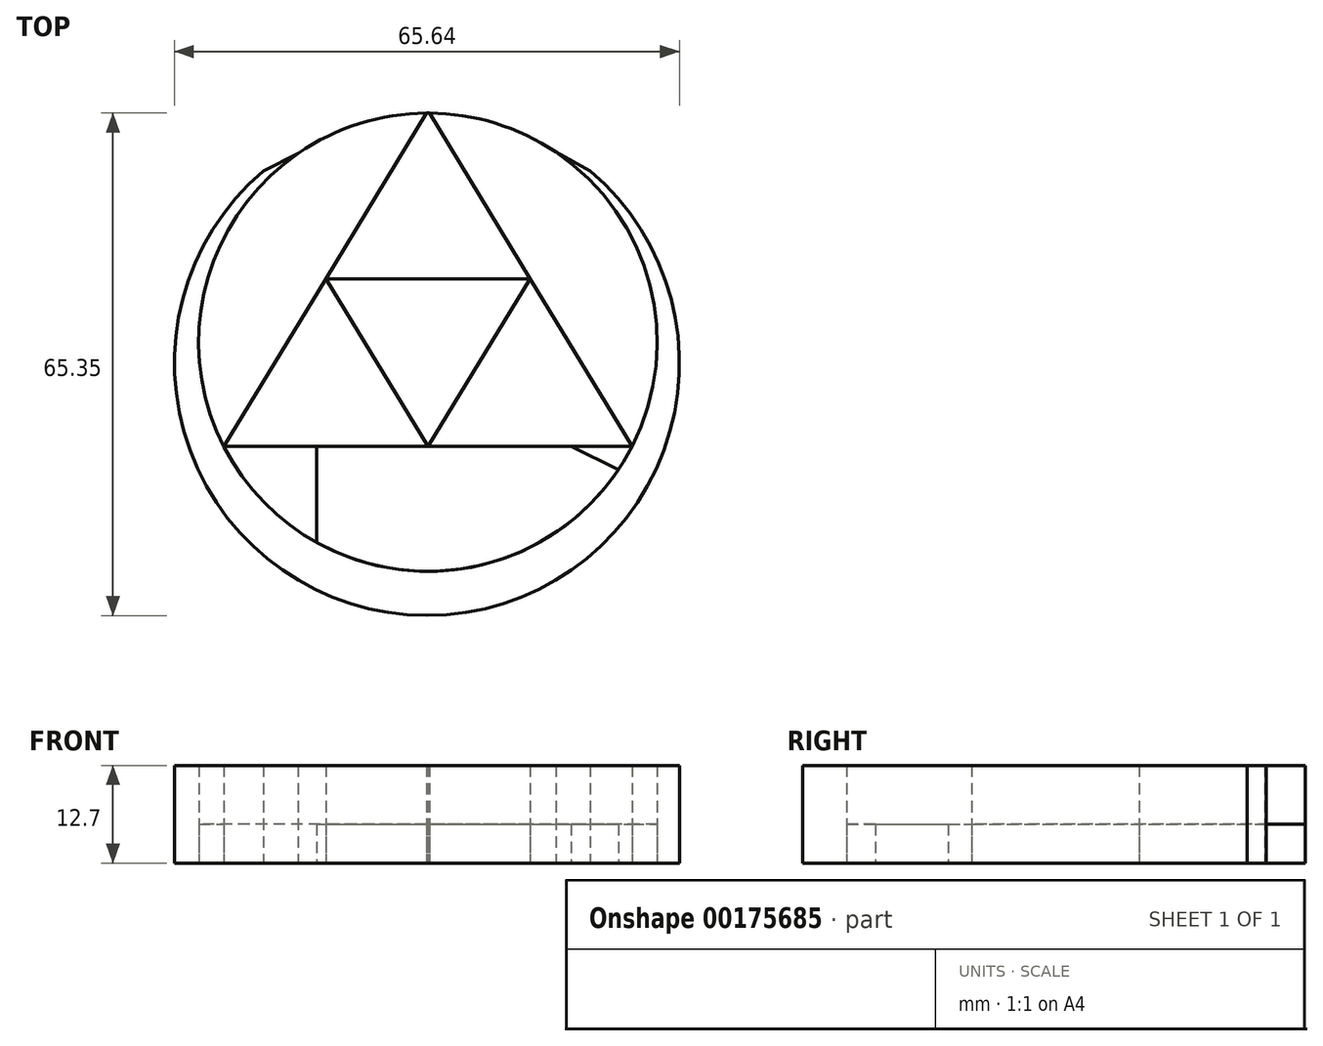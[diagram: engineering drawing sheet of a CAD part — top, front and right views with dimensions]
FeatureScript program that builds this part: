
annotation { "Feature Type Name" : "Feature", "Feature Type Description" : "" }
export const myFeature = defineFeature(function(context is Context, id is Id, definition is map)
    precondition{}
    {
        {
            var Q0;
            Q0=qCreatedBy(makeId("Top.planeOp"),FACE);
            var sketch = newSketch(context, id + "F0", { "sketchPlane" : qUnion([Q0])});
            skCircle(sketch, "E0", {"center": v(-14, 9.39) * mm, "radius": 29.8 * mm});
            skLineSegment(sketch, "E1", {"start": v(-40.55, -4.17) * mm, "end": v(12.54, -4.17) * mm});
            skLineSegment(sketch, "E2.bottom", {"start": v(-40.55, -4.17) * mm, "end": v(12.55, -4.17) * mm});
            skLineSegment(sketch, "E2.right", {"start": v(12.55, -4.17) * mm, "end": v(12.55, -4.16) * mm});
            skLineSegment(sketch, "E3", {"start": v(-14, 39.48) * mm, "end": v(-40.55, -4.17) * mm});
            skLineSegment(sketch, "E4", {"start": v(-14, 39.48) * mm, "end": v(12.54, -4.17) * mm});
            skPoint(sketch, "E5.orphan", {"position": v(-40.55, 39.48) * mm});
            skPoint(sketch, "E6.orphan", {"position": v(12.54, 39.48) * mm});
            skLineSegment(sketch, "E7", {"start": v(-27.27, 17.66) * mm, "end": v(-0.73, 17.66) * mm});
            skLineSegment(sketch, "E8", {"start": v(-0.73, 17.66) * mm, "end": v(-14, -4.17) * mm});
            skLineSegment(sketch, "E9", {"start": v(-14, -4.17) * mm, "end": v(-27.27, 17.66) * mm});
            skArc(sketch, "E10", {"start": v(-35.38, 31.68) * mm, "mid": v(-14.14, -26.16) * mm, "end": v(7.1, 31.68) * mm});
            skPoint(sketch, "E10.second.point", {"position": v(-14, -26.16) * mm});
            skPoint(sketch, "E10.third.point", {"position": v(15.75, -6.9) * mm});
            skPoint(sketch, "E11.middle", {"position": v(-14, -20.42) * mm});
            skPoint(sketch, "E12.orphan", {"position": v(-24.56, 2.87) * mm});
            skLineSegment(sketch, "E13.trimOffspring", {"start": v(-24.56, -4.17) * mm, "end": v(-24.56, -4.17) * mm});
            skLineSegment(sketch, "E14.trimOffspring", {"start": v(-3.44, -4.17) * mm, "end": v(-3.44, -4.17) * mm});
            skPoint(sketch, "E15.trimOffspring.end.orphan", {"position": v(-3.44, 2.87) * mm});
            skPoint(sketch, "E11.bottom.start.orphan", {"position": v(-24.56, -43.7) * mm});
            skPoint(sketch, "E11.right.start.orphan", {"position": v(-3.44, -43.7) * mm});
            skLineSegment(sketch, "E16.left", {"start": v(-10.35, -56.05) * mm, "end": v(-9.1, -67.57) * mm});
            skLineSegment(sketch, "E16.right", {"start": v(-19.53, -55.34) * mm, "end": v(-18.29, -66.87) * mm});
            skPoint(sketch, "E16.middle", {"position": v(-14.32, -61.46) * mm});
            skPoint(sketch, "E16.cornerSnap0", {"position": v(-28.46, -56.05) * mm});
            skPoint(sketch, "E17.orphan", {"position": v(-28.46, -61.9) * mm});
            skPoint(sketch, "E18.orphan", {"position": v(-0.18, -61.01) * mm});
            skLineSegment(sketch, "E19", {"start": v(-35.38, 31.68) * mm, "end": v(-30.87, 33.96) * mm});
            skLineSegment(sketch, "E20", {"start": v(7.1, 31.68) * mm, "end": v(2.63, 34.12) * mm});
            skPoint(sketch, "E21.middle", {"position": v(-13.7, -67.22) * mm});
            skPoint(sketch, "E21.right.end.orphan", {"position": v(-22.4, -64) * mm});
            skPoint(sketch, "E21.left.end.orphan", {"position": v(-5.12, -63.93) * mm});
            skPoint(sketch, "E21.bottom.end.orphan", {"position": v(-22.28, -70.52) * mm});
            skPoint(sketch, "E21.bottom.start.orphan", {"position": v(-5, -70.45) * mm});
            skLineSegment(sketch, "E22", {"start": v(-18.29, -66.87) * mm, "end": v(-22.28, -70.52) * mm});
            skLineSegment(sketch, "E23", {"start": v(-9.1, -67.57) * mm, "end": v(-5, -70.45) * mm});
            skLineSegment(sketch, "E24", {"start": v(-5, -70.45) * mm, "end": v(-13.7, -102.19) * mm});
            skLineSegment(sketch, "E25", {"start": v(-13.7, -102.19) * mm, "end": v(-22.28, -70.52) * mm});
            skLineSegment(sketch, "E26.right", {"start": v(-28.47, -16.67) * mm, "end": v(-28.47, -2.12) * mm});
            skLineSegment(sketch, "E27.trimOffspring", {"start": v(10.76, -7.2) * mm, "end": v(0.46, -2.12) * mm});
            skPoint(sketch, "E26.bottom.end.orphan", {"position": v(-28.46, -50.2) * mm});
            skPoint(sketch, "E26.bottom.start.orphan", {"position": v(0.46, -50.2) * mm});
            skLineSegment(sketch, "E28", {"start": v(-19.53, -55.34) * mm, "end": v(-28.46, -50.2) * mm});
            skLineSegment(sketch, "E29", {"start": v(-14, -26.16) * mm, "end": v(-28.46, -50.2) * mm});
            skLineSegment(sketch, "E30", {"start": v(0.46, -50.2) * mm, "end": v(-14, -26.16) * mm});
            skLineSegment(sketch, "E31", {"start": v(0.46, -50.2) * mm, "end": v(-10.35, -56.05) * mm});
            skPoint(sketch, "E32.right.end.orphan", {"position": v(-0.18, -45.42) * mm});
            skSolve(sketch);
        }
        {
            var Q0;
            {var subQ5=sQuery(id+"F0.wireOp",EDGE,"E7");Q0=makeQuery(id+"F0.imprint","IMPRINT",FACE,{"disambiguationData":[TD([[makeQuery(id+"F0.imprint","IMPRINT",EDGE,{"derivedFrom":subQ5}),1.0]])]});}
            var Q1;
            {var subQ1=sQuery(id+"F0.wireOp",EDGE,"E1");var subQ3=makeQuery(id+"F0.imprint","INTERSECT",VERTEX,{"derivedFrom":[subQ1,sQuery(id+"F0.wireOp",EDGE,"E13.trimOffspring")]});Q1=makeQuery(id+"F0.imprint","IMPRINT",FACE,{"disambiguationData":[TD([[makeQuery(id+"F0.imprint","IMPRINT",EDGE,{"disambiguationData":[TD([[subQ3,-1.0]])],"derivedFrom":subQ1}),1.0]])]});}
            var Q2;
            {var subQ0=sQuery(id+"F0.wireOp",EDGE,"E1");var subQ1=makeQuery(id+"F0.imprint","INTERSECT",VERTEX,{"derivedFrom":[subQ0,sQuery(id+"F0.wireOp",EDGE,"E14.trimOffspring")]});Q2=makeQuery(id+"F0.imprint","IMPRINT",FACE,{"disambiguationData":[TD([[makeQuery(id+"F0.imprint","IMPRINT",EDGE,{"disambiguationData":[TD([[subQ1,1.0]])],"derivedFrom":subQ0}),1.0]])]});}
            var Q3;
            Q3=makeQuery(id+"F0.imprint","IMPRINT",FACE,{"disambiguationData":[TD([[makeQuery(id+"F0.imprint","IMPRINT",EDGE,{"derivedFrom":sQuery(id+"F0.wireOp",EDGE,"QvcDBj8m-urHB-6KoM-OWGO-5g0VVoQY0J0B")}),1.0]])]});
            var Q4;
            {var subQ0=sQuery(id+"F0.wireOp",EDGE,"E2.right");Q4=makeQuery(id+"F0.imprint","IMPRINT",FACE,{"disambiguationData":[TD([[makeQuery(id+"F0.imprint","IMPRINT",EDGE,{"derivedFrom":subQ0}),-1.0]])]});}
            extrude(context, id + "F1", {"entities" : qUnion([Q0, Q1, Q2, Q3, Q4]), "depth" : 12.7 * mm});
        }
        {
            var Q0;
            {var subQ5=sQuery(id+"F0.wireOp",EDGE,"E7");Q0=makeQuery(id+"F0.imprint","IMPRINT",FACE,{"disambiguationData":[TD([[makeQuery(id+"F0.imprint","IMPRINT",EDGE,{"derivedFrom":subQ5}),-1.0]])]});}
            var Q1;
            {var subQ0=sQuery(id+"F0.wireOp",EDGE,"E2.bottom");var subQ2=makeQuery(id+"F0.imprint","INTERSECT",VERTEX,{"derivedFrom":[subQ0,sQuery(id+"F0.wireOp",EDGE,"E14.trimOffspring")]});Q1=makeQuery(id+"F0.imprint","IMPRINT",FACE,{"disambiguationData":[TD([[makeQuery(id+"F0.imprint","IMPRINT",EDGE,{"disambiguationData":[TD([[subQ2,-1.0]])],"derivedFrom":subQ0}),-1.0]])]});}
            var Q2;
            {var subQ0=sQuery(id+"F0.wireOp",EDGE,"E0");var subQ1=makeQuery(id+"F0.imprint","INTERSECT",VERTEX,{"derivedFrom":[subQ0,sQuery(id+"F0.wireOp",EDGE,"E19")]});Q2=makeQuery(id+"F0.imprint","IMPRINT",FACE,{"disambiguationData":[TD([[makeQuery(id+"F0.imprint","IMPRINT",EDGE,{"disambiguationData":[TD([[subQ1,1.0]])],"derivedFrom":subQ0}),1.0]])]});}
            var Q3;
            {var subQ0=sQuery(id+"F0.wireOp",EDGE,"E0");var subQ2=makeQuery(id+"F0.imprint","INTERSECT",VERTEX,{"derivedFrom":[subQ0,sQuery(id+"F0.wireOp",EDGE,"E20")]});Q3=makeQuery(id+"F0.imprint","IMPRINT",FACE,{"disambiguationData":[TD([[makeQuery(id+"F0.imprint","IMPRINT",EDGE,{"disambiguationData":[TD([[subQ2,-1.0]])],"derivedFrom":subQ0}),1.0]])]});}
            extrude(context, id + "F2", {"entities" : qUnion([Q0, Q1, Q2, Q3]), "depth" : 5.08 * mm});
        }
    });
